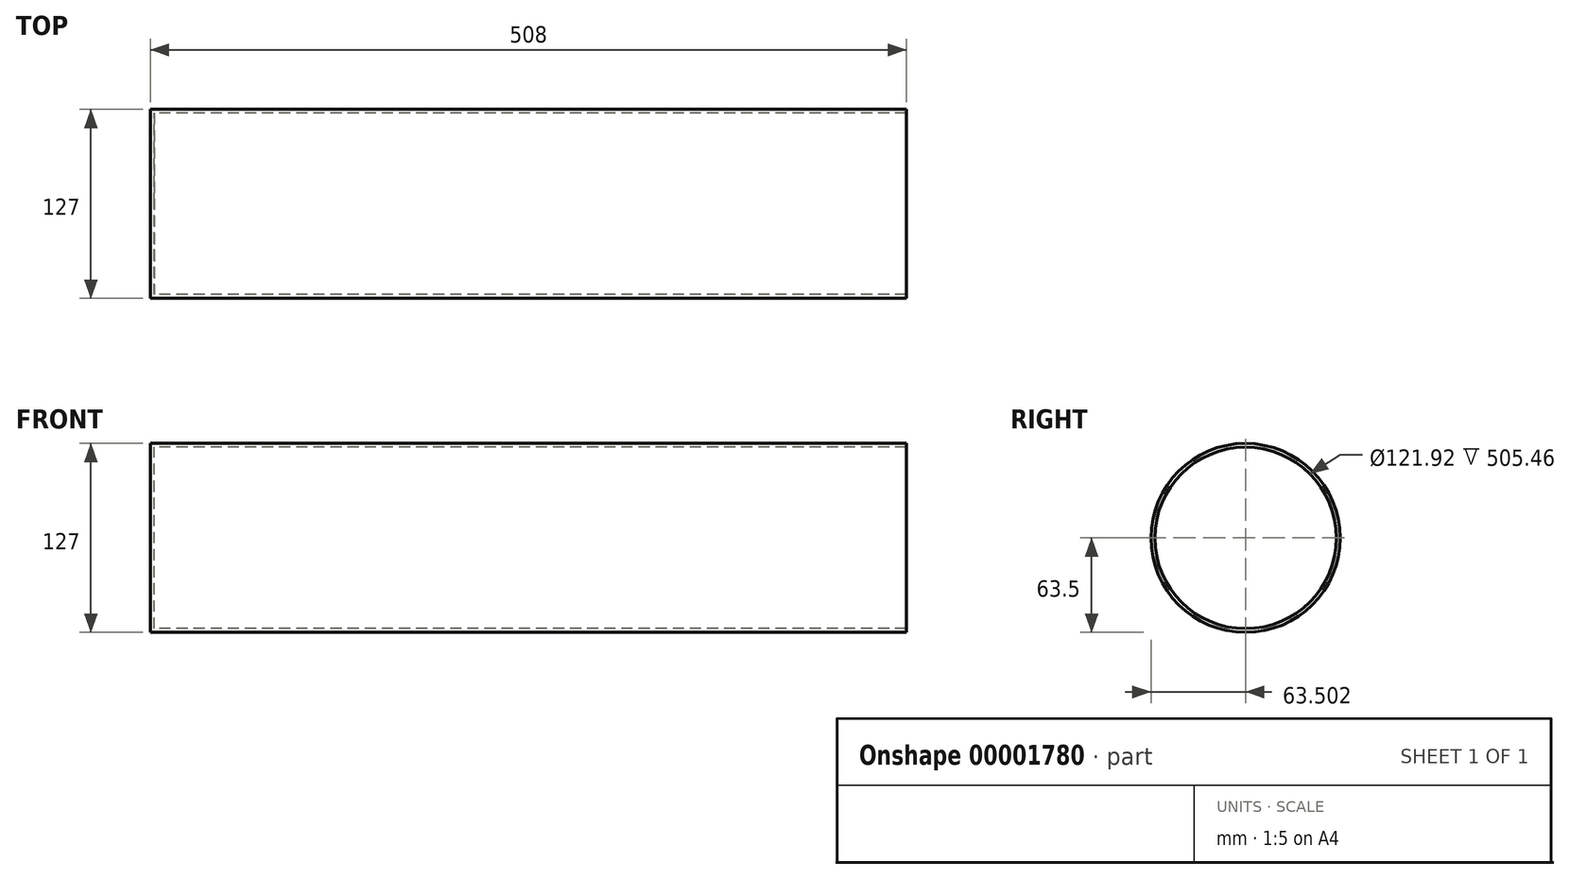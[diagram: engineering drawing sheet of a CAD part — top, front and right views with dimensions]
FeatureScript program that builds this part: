
annotation { "Feature Type Name" : "Feature", "Feature Type Description" : "" }
export const myFeature = defineFeature(function(context is Context, id is Id, definition is map)
    precondition{}
    {
        {
            var Q0;
            Q0=qCreatedBy(makeId("Right.planeOp"),FACE);
            var sketch = newSketch(context, id + "F0", { "sketchPlane" : qUnion([Q0])});
            skCircle(sketch, "E0", {"center": v(0.83, 0) * mm, "radius": 63.5 * mm});
            skArc(sketch, "E1.trimOffspring", {"start": v(30.3, -56.25) * mm, "mid": v(36.62, -52.92) * mm, "end": v(42.06, -48.3) * mm});
            skSolve(sketch);
        }
        {
            var Q0;
            {var subQ0=sQuery(id+"F0.wireOp",EDGE,"E0");var subQ1=sQuery(id+"F0.wireOp",EDGE,"E1.trimOffspring");var subQ3=makeQuery(id+"F0.imprint","INTERSECT",VERTEX,{"disambiguationData":[OD(0.0)],"derivedFrom":[subQ0,subQ1]});Q0=makeQuery(id+"F0.imprint","IMPRINT",FACE,{"disambiguationData":[TD([[makeQuery(id+"F0.imprint","IMPRINT",EDGE,{"disambiguationData":[TD([[subQ3,-1.0]])],"derivedFrom":subQ0}),1.0]])]});}
            extrude(context, id + "F1", {"entities" : qUnion([Q0]), "endBound" : BoundingType.SYMMETRIC, "depth" : 508 * mm});
        }
        {
            var Q0;
            Q0=makeQuery(id+"F1.opExtrude","CAP_FACE",FACE,{"disambiguationData":[OSD([sQuery(id+"F0.wireOp",EDGE,"E0")])],"isStart":false});
            shell(context, id + "F2", {"entities" : qUnion([Q0]), "thickness" : 2.54 * mm});
        }
    });
